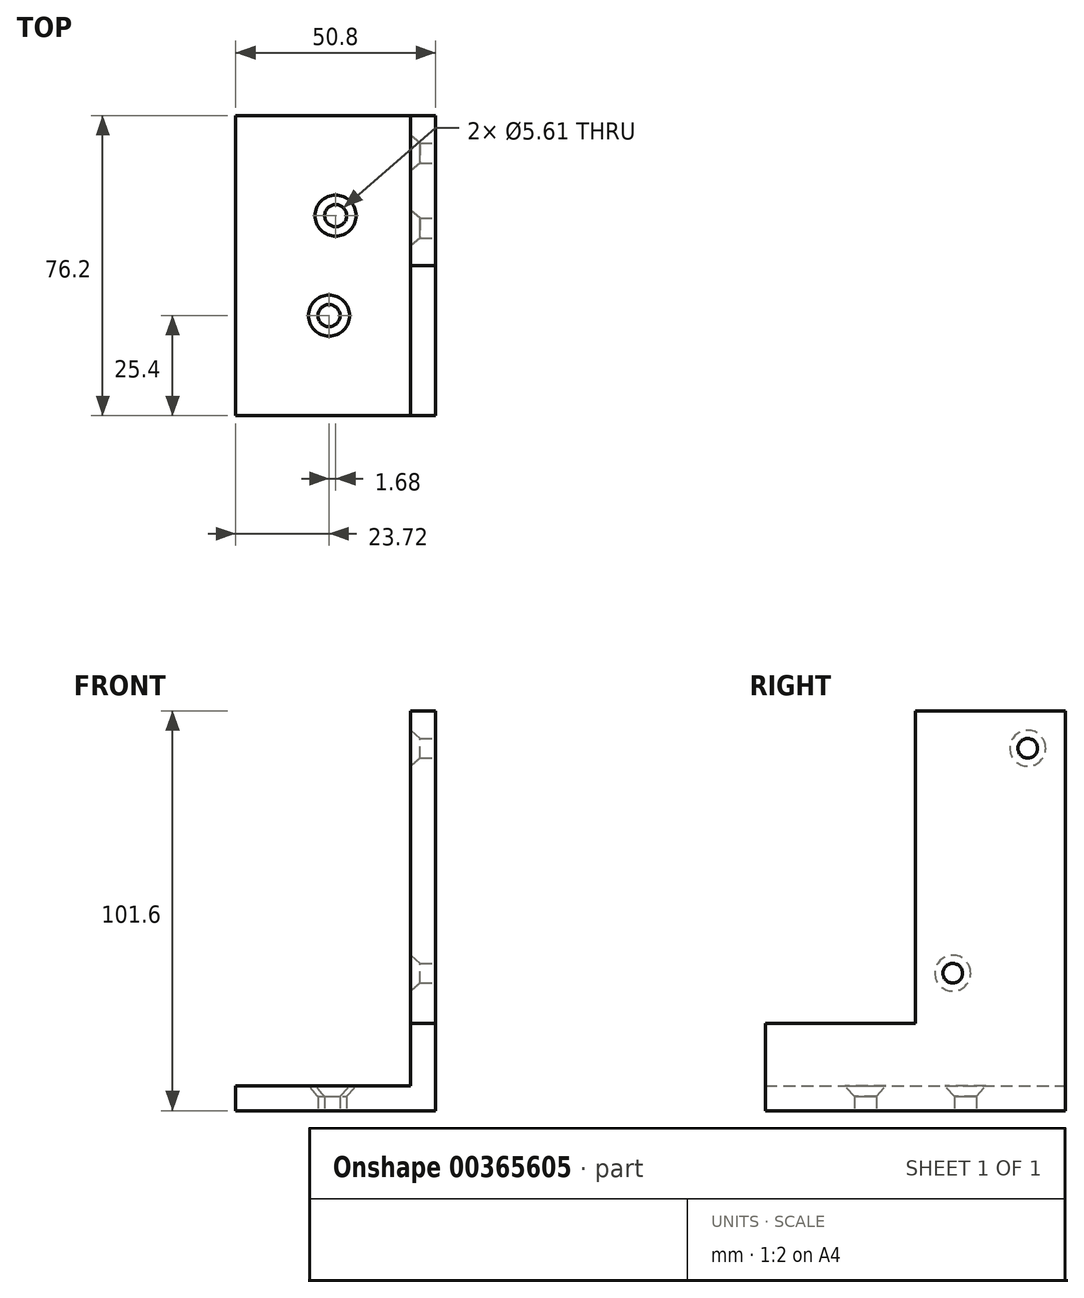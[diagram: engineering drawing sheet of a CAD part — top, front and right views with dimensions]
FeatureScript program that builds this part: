
annotation { "Feature Type Name" : "Feature", "Feature Type Description" : "" }
export const myFeature = defineFeature(function(context is Context, id is Id, definition is map)
    precondition{}
    {
        {
            var Q0;
            Q0=qCreatedBy(makeId("Front.planeOp"),FACE);
            var sketch = newSketch(context, id + "F0", { "sketchPlane" : qUnion([Q0])});
            skLineSegment(sketch, "E0", {"start": v(0, 0) * mm, "end": v(0, 101.6) * mm});
            skLineSegment(sketch, "E1", {"start": v(0, 101.6) * mm, "end": v(-6.35, 101.6) * mm});
            skLineSegment(sketch, "E2", {"start": v(-6.35, 101.6) * mm, "end": v(-6.35, 6.35) * mm});
            skLineSegment(sketch, "E3", {"start": v(-6.35, 6.35) * mm, "end": v(-50.8, 6.35) * mm});
            skLineSegment(sketch, "E4", {"start": v(-50.8, 6.35) * mm, "end": v(-50.8, 0) * mm});
            skLineSegment(sketch, "E5", {"start": v(-50.8, 0) * mm, "end": v(0, 0) * mm});
            skSolve(sketch);
        }
        {
            var Q0;
            Q0=qSketchRegion(id+"F0",true);
            extrude(context, id + "F1", {"entities" : qUnion([Q0]), "depth" : 76.2 * mm, "offsetDistance" : 25.4 * mm});
        }
        {
            var Q0;
            Q0=makeQuery(id+"F1.opExtrude","SWEPT_FACE",FACE,{"disambiguationData":[OSD([sQuery(id+"F0.wireOp",EDGE,"E2")])]});
            var sketch = newSketch(context, id + "F2", { "sketchPlane" : qUnion([Q0])});
            skPoint(sketch, "E6", {"position": v(9.53, 92.07) * mm});
            skPoint(sketch, "E7", {"position": v(28.58, 34.92) * mm});
            skSolve(sketch);
        }
        {
            var Q0;
            Q0=sQuery(id+"F2.wireOp",VERTEX,"E6");
            var Q1;
            Q1=sQuery(id+"F2.wireOp",VERTEX,"E7");
            var Q2;
            Q2=makeQuery(id+"F1.opExtrude","SWEPT_BODY",BODY,{"disambiguationData":[OSD([sQuery(id+"F0.wireOp",EDGE,"E0"),sQuery(id+"F0.wireOp",EDGE,"E1"),sQuery(id+"F0.wireOp",EDGE,"E2"),sQuery(id+"F0.wireOp",EDGE,"E3"),sQuery(id+"F0.wireOp",EDGE,"E4"),sQuery(id+"F0.wireOp",EDGE,"E5")])]});
            hole(context, id + "F3", {"style" : HoleStyle.C_SINK, "endStyle" : HoleEndStyle.THROUGH, "standardTappedOrClearance" : lookupTablePath({ "fit" : "Normal (ASME)", "standard" : "ANSI", "size" : "#8", "type" : "Clearance" }), "standardBlindInLast" : lookupTablePath({ "fit" : "Normal", "standard" : "ANSI", "engagement" : "75%", "pitch" : "32 tpi", "size" : "#8", "type" : "Clearance & tapped" }), "holeDiameter" : 4.98 * mm, "cSinkDiameter" : 9.12 * mm, "cSinkAngle" : 82 * degree, "majorDiameter" : 6.35 * mm, "isTappedThrough" : true, "tappedDepth" : 12.7 * mm, "tapClearance" : 3, "locations" : qUnion([Q0, Q1]), "scope" : qUnion([Q2]), "startStyle" : HoleStartStyle.SKETCH});
        }
        {
            var Q0;
            Q0=makeQuery(id+"F1.opExtrude","SWEPT_FACE",FACE,{"disambiguationData":[OSD([sQuery(id+"F0.wireOp",EDGE,"E3")])]});
            var sketch = newSketch(context, id + "F4", { "sketchPlane" : qUnion([Q0])});
            skPoint(sketch, "E8", {"position": v(-27.08, -50.8) * mm});
            skPoint(sketch, "E9", {"position": v(-25.4, -25.4) * mm});
            skSolve(sketch);
        }
        {
            var Q0;
            Q0=sQuery(id+"F4.wireOp",VERTEX,"E9");
            var Q1;
            Q1=sQuery(id+"F4.wireOp",VERTEX,"E8");
            var Q2;
            Q2=makeQuery(id+"F1.opExtrude","SWEPT_BODY",BODY,{"disambiguationData":[OSD([sQuery(id+"F0.wireOp",EDGE,"E0"),sQuery(id+"F0.wireOp",EDGE,"E1"),sQuery(id+"F0.wireOp",EDGE,"E2"),sQuery(id+"F0.wireOp",EDGE,"E3"),sQuery(id+"F0.wireOp",EDGE,"E4"),sQuery(id+"F0.wireOp",EDGE,"E5")])]});
            hole(context, id + "F5", {"style" : HoleStyle.C_SINK, "endStyle" : HoleEndStyle.THROUGH, "standardTappedOrClearance" : lookupTablePath({ "fit" : "Normal (ASME)", "standard" : "ANSI", "size" : "#10", "type" : "Clearance" }), "standardBlindInLast" : lookupTablePath({ "fit" : "Normal", "standard" : "ANSI", "engagement" : "75%", "pitch" : "24 tpi", "size" : "#10", "type" : "Clearance & tapped" }), "holeDiameter" : 5.61 * mm, "cSinkDiameter" : 10.44 * mm, "cSinkAngle" : 82 * degree, "majorDiameter" : 6.35 * mm, "isTappedThrough" : true, "tappedDepth" : 12.7 * mm, "tapClearance" : 3, "locations" : qUnion([Q0, Q1]), "scope" : qUnion([Q2]), "startStyle" : HoleStartStyle.SKETCH});
        }
        {
            var Q0;
            Q0=makeQuery(id+"F1.opExtrude","SWEPT_FACE",FACE,{"disambiguationData":[OSD([sQuery(id+"F0.wireOp",EDGE,"E2")])]});
            var sketch = newSketch(context, id + "F6", { "sketchPlane" : qUnion([Q0])});
            skLineSegment(sketch, "E10.bottom", {"start": v(76.2, 101.6) * mm, "end": v(38.1, 101.6) * mm});
            skLineSegment(sketch, "E10.top", {"start": v(76.2, 22.22) * mm, "end": v(38.1, 22.22) * mm});
            skLineSegment(sketch, "E10.left", {"start": v(76.2, 101.6) * mm, "end": v(76.2, 22.22) * mm});
            skLineSegment(sketch, "E10.right", {"start": v(38.1, 101.6) * mm, "end": v(38.1, 22.23) * mm});
            skSolve(sketch);
        }
        {
            var Q0;
            Q0=makeQuery(id+"F6.imprint","IMPRINT",FACE,{"disambiguationData":[TD([[makeQuery(id+"F6.imprint","IMPRINT",EDGE,{"derivedFrom":sQuery(id+"F6.wireOp",EDGE,"56uQzYml-uIxs-i8ak-qa3T-DG6t4iAps5dJ.bottom")}),1.0]])]});
            var Q1;
            Q1=makeQuery(id+"F6.imprint","IMPRINT",FACE,{"disambiguationData":[TD([[makeQuery(id+"F6.imprint","IMPRINT",EDGE,{"derivedFrom":sQuery(id+"F6.wireOp",EDGE,"E10.bottom")}),1.0]])]});
            extrude(context, id + "F7", {"entities" : qUnion([Q0, Q1]), "operationType" : NewBodyOperationType.REMOVE, "endBound" : BoundingType.THROUGH_ALL, "oppositeDirection" : true, "depth" : 25.4 * mm, "offsetDistance" : 25.4 * mm});
        }
    });
